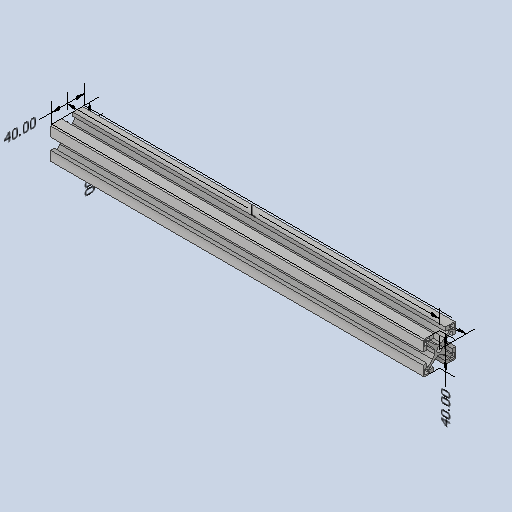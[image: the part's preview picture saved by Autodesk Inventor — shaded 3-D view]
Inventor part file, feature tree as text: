
AUTODESK INVENTOR PART (.ipt)
format: ipt  version: 2023 (Build 270158000, 158)  size: 274,944 bytes
history: native  units: mm
features: other x125, extrude x1, sketch x1
ambient origin geometry x8: Origin, YZ Plane, XZ Plane, XY Plane, X Axis, Y Axis, Z Axis, Center Point
bodies: Solid1 (feature_tree)
feature tree (127):
  other  "Annotations"
  extrude  "Extrusion1"  [1 undecoded]
  other  "CS_ANBAU_HINTEN_LINKS_XY"
  other  "CS_ANBAU_HINTEN_LINKS_YZ"
  other  "CS_ANBAU_HINTEN_LINKS_ZX"
  other  "CS_ANBAU_HINTEN_LINKS_X"
  other  "CS_ANBAU_HINTEN_LINKS_Y"
  other  "CS_ANBAU_HINTEN_LINKS_Z"
  other  "CS_ANBAU_HINTEN_LINKS_Center"
  other  "CS_ANBAU_HINTEN_OBEN_XY"
  other  "CS_ANBAU_HINTEN_OBEN_YZ"
  other  "CS_ANBAU_HINTEN_OBEN_ZX"
  other  "CS_ANBAU_HINTEN_OBEN_X"
  other  "CS_ANBAU_HINTEN_OBEN_Y"
  other  "CS_ANBAU_HINTEN_OBEN_Z"
  other  "CS_ANBAU_HINTEN_OBEN_Center"
  other  "CS_ANBAU_HINTEN_RECHTS_XY"
  other  "CS_ANBAU_HINTEN_RECHTS_YZ"
  other  "CS_ANBAU_HINTEN_RECHTS_ZX"
  other  "CS_ANBAU_HINTEN_RECHTS_X"
  other  "CS_ANBAU_HINTEN_RECHTS_Y"
  other  "CS_ANBAU_HINTEN_RECHTS_Z"
  other  "CS_ANBAU_HINTEN_RECHTS_Center"
  other  "CS_ANBAU_HINTEN_UNTEN_XY"
  other  "CS_ANBAU_HINTEN_UNTEN_YZ"
  other  "CS_ANBAU_HINTEN_UNTEN_ZX"
  other  "CS_ANBAU_HINTEN_UNTEN_X"
  other  "CS_ANBAU_HINTEN_UNTEN_Y"
  other  "CS_ANBAU_HINTEN_UNTEN_Z"
  other  "CS_ANBAU_HINTEN_UNTEN_Center"
  other  "CS_ANBAU_QUER_XY"
  other  "CS_ANBAU_QUER_YZ"
  other  "CS_ANBAU_QUER_ZX"
  other  "CS_ANBAU_QUER_X"
  other  "CS_ANBAU_QUER_Y"
  other  "CS_ANBAU_QUER_Z"
  other  "CS_ANBAU_QUER_Center"
  other  "CS_ANBAU_QUER_1_XY"
  other  "CS_ANBAU_QUER_1_YZ"
  other  "CS_ANBAU_QUER_1_ZX"
  other  "CS_ANBAU_QUER_1_X"
  other  "CS_ANBAU_QUER_1_Y"
  other  "CS_ANBAU_QUER_1_Z"
  other  "CS_ANBAU_QUER_1_Center"
  other  "CS_ANBAU_VORNE_LINKS_XY"
  other  "CS_ANBAU_VORNE_LINKS_YZ"
  other  "CS_ANBAU_VORNE_LINKS_ZX"
  other  "CS_ANBAU_VORNE_LINKS_X"
  other  "CS_ANBAU_VORNE_LINKS_Y"
  other  "CS_ANBAU_VORNE_LINKS_Z"
  other  "CS_ANBAU_VORNE_LINKS_Center"
  other  "CS_ANBAU_VORNE_OBEN_XY"
  other  "CS_ANBAU_VORNE_OBEN_YZ"
  other  "CS_ANBAU_VORNE_OBEN_ZX"
  other  "CS_ANBAU_VORNE_OBEN_X"
  other  "CS_ANBAU_VORNE_OBEN_Y"
  other  "CS_ANBAU_VORNE_OBEN_Z"
  other  "CS_ANBAU_VORNE_OBEN_Center"
  other  "CS_ANBAU_VORNE_RECHTS_XY"
  other  "CS_ANBAU_VORNE_RECHTS_YZ"
  other  "CS_ANBAU_VORNE_RECHTS_ZX"
  other  "CS_ANBAU_VORNE_RECHTS_X"
  other  "CS_ANBAU_VORNE_RECHTS_Y"
  other  "CS_ANBAU_VORNE_RECHTS_Z"
  other  "CS_ANBAU_VORNE_RECHTS_Center"
  other  "CS_ANBAU_VORNE_UNTEN_XY"
  other  "CS_ANBAU_VORNE_UNTEN_YZ"
  other  "CS_ANBAU_VORNE_UNTEN_ZX"
  other  "CS_ANBAU_VORNE_UNTEN_X"
  other  "CS_ANBAU_VORNE_UNTEN_Y"
  other  "CS_ANBAU_VORNE_UNTEN_Z"
  other  "CS_ANBAU_VORNE_UNTEN_Center"
  other  "p1_XY"
  other  "p1_YZ"
  other  "p1_ZX"
  other  "p1_X"
  other  "p1_Y"
  other  "p1_Z"
  other  "p1_Center"
  other  "p2_XY"
  other  "p2_YZ"
  other  "p2_ZX"
  other  "p2_X"
  other  "p2_Y"
  other  "p2_Z"
  other  "p2_Center"
  other  "p3_XY"
  other  "p3_YZ"
  other  "p3_ZX"
  other  "p3_X"
  other  "p3_Y"
  other  "p3_Z"
  other  "p3_Center"
  other  "p4_XY"
  other  "p4_YZ"
  other  "p4_ZX"
  other  "p4_X"
  other  "p4_Y"
  other  "p4_Z"
  other  "p4_Center"
  other  "p5_XY"
  other  "p5_YZ"
  other  "p5_ZX"
  other  "p5_X"
  other  "p5_Y"
  other  "p5_Z"
  other  "p5_Center"
  other  "pm1_XY"
  other  "pm1_YZ"
  other  "pm1_ZX"
  other  "pm1_X"
  other  "pm1_Y"
  other  "pm1_Z"
  other  "pm1_Center"
  other  "pm2_XY"
  other  "pm2_YZ"
  other  "pm2_ZX"
  other  "pm2_X"
  other  "pm2_Y"
  other  "pm2_Z"
  other  "pm2_Center"
  sketch  "Skizze_1"  dims[d0=456.0mm d1=0.0mm d2=0.0mm d3=0.0mm d4=0.0mm d5=0.0mm d6=0.0mm d10=456.0mm d11=456.0mm d7=40.0mm d8=40.0mm d9=40.0mm]
  other  "Linear Dimension 1"
  other  "Linear Dimension 2"
  other  "Linear Dimension 3"
  other  "Linear Dimension 4"
  other  "Linear Dimension 5"
note: 1 required parameter value undecoded (feature->parameter linkage not recoverable at this tier; creation-order binding heuristic only, values carry confidence <= 0.55)
